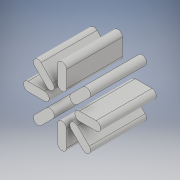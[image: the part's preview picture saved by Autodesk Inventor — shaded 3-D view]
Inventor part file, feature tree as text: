
AUTODESK INVENTOR PART (.ipt)
format: ipt  version: 2019 (Build 230136000, 136)  size: 333,312 bytes
history: native  units: mm
features: extrude x1, sketch x1
ambient origin geometry x8: Origin, YZ Plane, XZ Plane, XY Plane, X Axis, Y Axis, Z Axis, Center Point
bodies: Solid1 (feature_tree)
feature tree (2):
  extrude  "Extrusion1"  Depth=50.0mm
  sketch  "Sketch1"  dims[d0=4.0mm d1=15.0mm d2=80.0mm d4=360.0deg d6=50.0mm d7=0.0mm]
